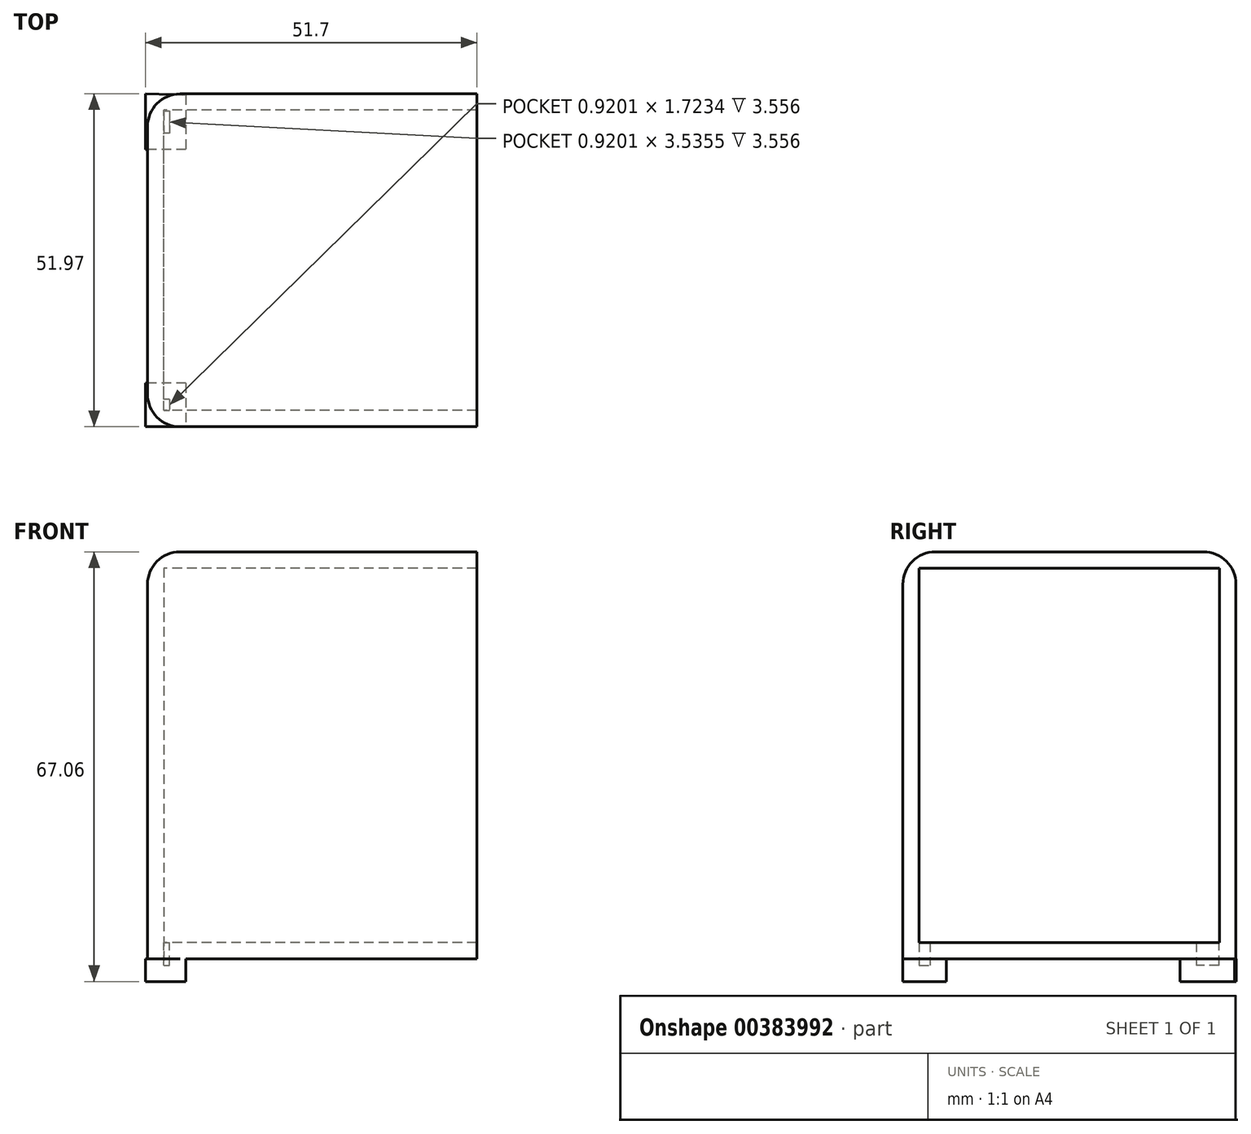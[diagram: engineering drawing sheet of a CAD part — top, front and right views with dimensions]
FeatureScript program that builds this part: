
annotation { "Feature Type Name" : "Feature", "Feature Type Description" : "" }
export const myFeature = defineFeature(function(context is Context, id is Id, definition is map)
    precondition{}
    {
        {
            var Q0;
            Q0=qCreatedBy(makeId("Top.planeOp"),FACE);
            var sketch = newSketch(context, id + "F0", { "sketchPlane" : qUnion([Q0])});
            skLineSegment(sketch, "E0.bottom", {"start": v(0, 0) * mm, "end": v(-51.37, 0) * mm});
            skLineSegment(sketch, "E0.top", {"start": v(0, 51.95) * mm, "end": v(-51.37, 51.95) * mm});
            skLineSegment(sketch, "E0.left", {"start": v(0, 0) * mm, "end": v(0, 51.95) * mm});
            skLineSegment(sketch, "E0.right", {"start": v(-51.37, 0) * mm, "end": v(-51.37, 51.95) * mm});
            skSolve(sketch);
        }
        {
            var Q0;
            Q0=makeQuery(id+"F0.imprint","IMPRINT",FACE,{"disambiguationData":[TD([[makeQuery(id+"F0.imprint","IMPRINT",EDGE,{"derivedFrom":sQuery(id+"F0.wireOp",EDGE,"E0.bottom")}),-1.0]])]});
            extrude(context, id + "F1", {"entities" : qUnion([Q0]), "depth" : 63.5 * mm, "offsetDistance" : 25.4 * mm});
        }
        {
            var Q0;
            Q0=qCreatedBy(makeId("Top.planeOp"),FACE);
            var sketch = newSketch(context, id + "F2", { "sketchPlane" : qUnion([Q0])});
            skLineSegment(sketch, "E1", {"start": v(-51.7, 0) * mm, "end": v(-51.7, 6.8) * mm});
            skLineSegment(sketch, "E2", {"start": v(-45.37, 6.8) * mm, "end": v(-45.37, 0) * mm});
            skLineSegment(sketch, "E3", {"start": v(-45.37, 6.8) * mm, "end": v(-51.7, 6.8) * mm});
            skLineSegment(sketch, "E4", {"start": v(-45.37, 51.76) * mm, "end": v(-45.37, 43.26) * mm});
            skLineSegment(sketch, "E5", {"start": v(-45.37, 43.26) * mm, "end": v(-51.7, 43.26) * mm});
            skLineSegment(sketch, "E6", {"start": v(-51.7, 43.26) * mm, "end": v(-51.7, 51.97) * mm});
            skLineSegment(sketch, "E7", {"start": v(-51.7, 0) * mm, "end": v(-45.37, 0) * mm});
            skLineSegment(sketch, "E8", {"start": v(-51.7, 51.97) * mm, "end": v(-51.7, 47.61) * mm});
            skLineSegment(sketch, "E9", {"start": v(-51.7, 6.8) * mm, "end": v(-51.7, 3.4) * mm});
            skLineSegment(sketch, "E10", {"start": v(-51.7, 51.97) * mm, "end": v(-45.37, 51.76) * mm});
            skSolve(sketch);
        }
        {
            var Q0;
            Q0 = qSketchRegion(id + "F2", true);
            extrude(context, id + "F3", {"entities" : qUnion([Q0]), "operationType" : NewBodyOperationType.ADD, "oppositeDirection" : true, "depth" : 3.56 * mm, "offsetDistance" : 25.4 * mm});
        }
        {
            var Q0;
            Q0=makeQuery(id+"F1.opExtrude","SWEPT_FACE",FACE,{"disambiguationData":[OSD([sQuery(id+"F0.wireOp",EDGE,"E0.left")])]});
            shell(context, id + "F4", {"entities" : qUnion([Q0]), "thickness" : 2.54 * mm});
        }
        {
            var Q0;
            Q0=makeQuery(id+"F1.opExtrude","SWEPT_EDGE",EDGE,{"disambiguationData":[OSD([sQuery(id+"F0.wireOp",EDGE,"E0.bottom"),sQuery(id+"F0.wireOp",EDGE,"E0.right")])]});
            var Q1;
            Q1=makeQuery(id+"F1.opExtrude","SWEPT_EDGE",EDGE,{"disambiguationData":[OSD([sQuery(id+"F0.wireOp",EDGE,"E0.top"),sQuery(id+"F0.wireOp",EDGE,"E0.right")])]});
            fillet(context, id + "F5", {"entities" : qUnion([Q0, Q1]), "radius" : 5.08 * mm, "tangentPropagation" : true, "allowEdgeOverflow" : false});
        }
        {
            var Q0;
            Q0=makeQuery(id+"F1.opExtrude","CAP_EDGE",EDGE,{"disambiguationData":[OSD([sQuery(id+"F0.wireOp",EDGE,"E0.right")])],"isStart":false});
            fillet(context, id + "F6", {"entities" : qUnion([Q0]), "radius" : 5.08 * mm, "tangentPropagation" : true, "allowEdgeOverflow" : false});
        }
    });
